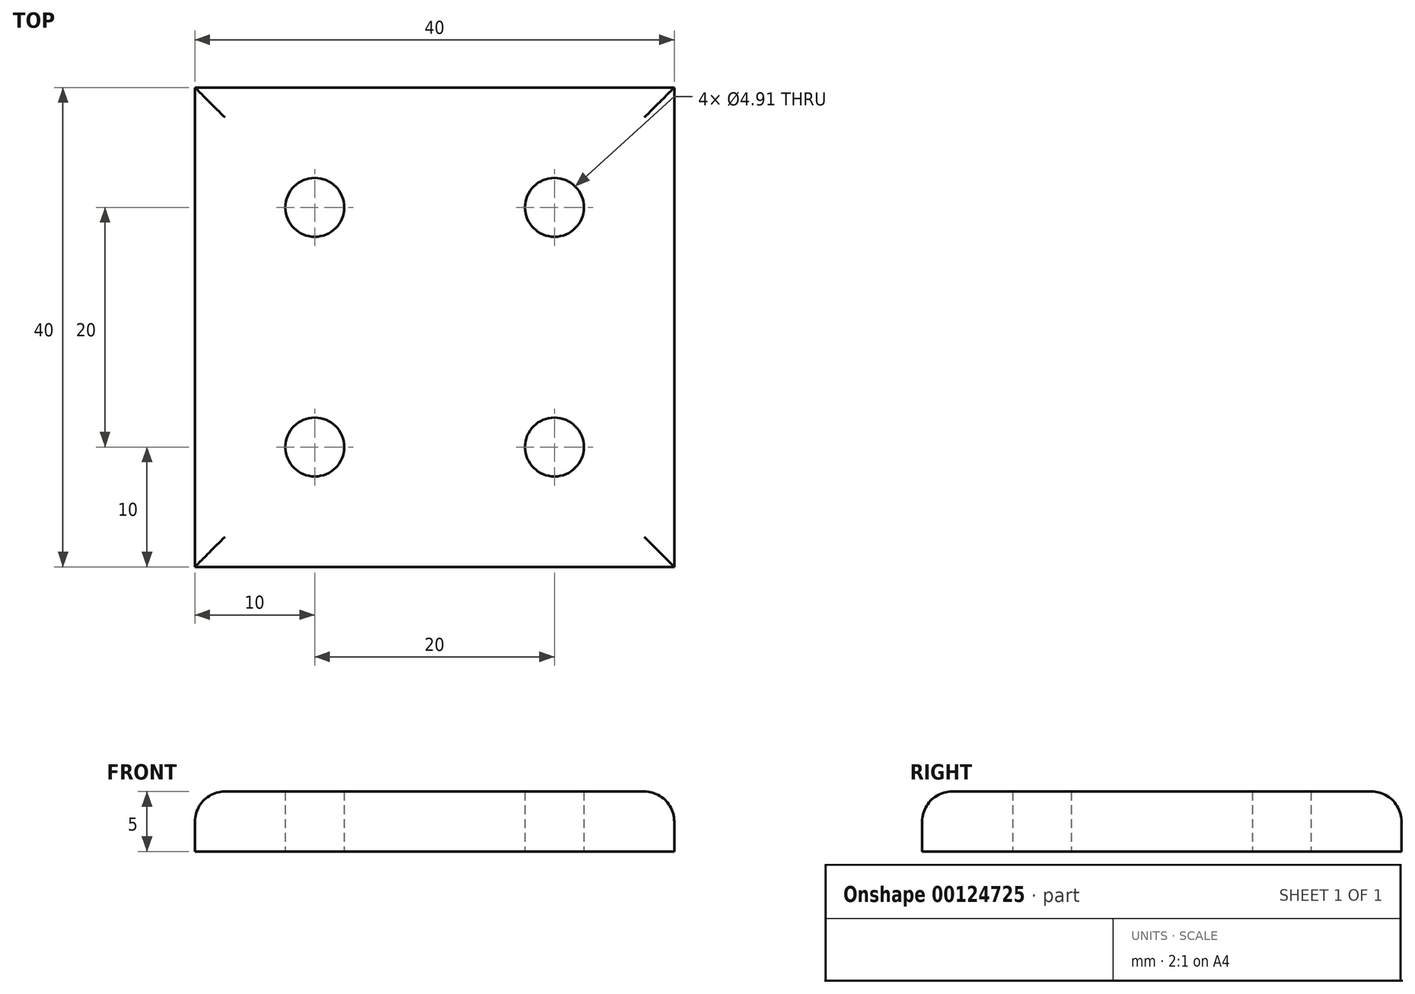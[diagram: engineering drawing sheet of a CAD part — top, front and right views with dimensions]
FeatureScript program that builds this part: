
annotation { "Feature Type Name" : "Feature", "Feature Type Description" : "" }
export const myFeature = defineFeature(function(context is Context, id is Id, definition is map)
    precondition{}
    {
        {
            var Q0;
            Q0=qCreatedBy(makeId("Top.planeOp"),FACE);
            var sketch = newSketch(context, id + "F0", { "sketchPlane" : qUnion([Q0])});
            skLineSegment(sketch, "E0.bottom", {"start": v(-20, 20) * mm, "end": v(20, 20) * mm});
            skLineSegment(sketch, "E0.top", {"start": v(-20, -20) * mm, "end": v(20, -20) * mm});
            skLineSegment(sketch, "E0.left", {"start": v(-20, 20) * mm, "end": v(-20, -20) * mm});
            skLineSegment(sketch, "E0.right", {"start": v(20, 20) * mm, "end": v(20, -20) * mm});
            skPoint(sketch, "E0.middle", {"position": v(0, 0) * mm});
            skCircle(sketch, "E1", {"center": v(-10, 10) * mm, "radius": 2.46 * mm});
            skCircle(sketch, "E2.1.0", {"center": v(-10, -10) * mm, "radius": 2.46 * mm});
            skCircle(sketch, "E2.2.0", {"center": v(10, -10) * mm, "radius": 2.46 * mm});
            skCircle(sketch, "E2.3.0", {"center": v(10, 10) * mm, "radius": 2.46 * mm});
            skSolve(sketch);
        }
        {
            var Q0;
            Q0=makeQuery(id+"F0.imprint","IMPRINT",FACE,{"disambiguationData":[TD([[makeQuery(id+"F0.imprint","IMPRINT",EDGE,{"derivedFrom":sQuery(id+"F0.wireOp",EDGE,"E0.bottom")}),-1.0]])]});
            extrude(context, id + "F1", {"entities" : qUnion([Q0]), "depth" : 5 * mm});
        }
        {
            var Q0;
            Q0=makeQuery(id+"F1.opExtrude","CAP_EDGE",EDGE,{"disambiguationData":[OSD([sQuery(id+"F0.wireOp",EDGE,"E0.top")])],"isStart":false});
            var Q1;
            Q1=makeQuery(id+"F1.opExtrude","CAP_EDGE",EDGE,{"disambiguationData":[OSD([sQuery(id+"F0.wireOp",EDGE,"E0.left")])],"isStart":false});
            var Q2;
            Q2=makeQuery(id+"F1.opExtrude","CAP_EDGE",EDGE,{"disambiguationData":[OSD([sQuery(id+"F0.wireOp",EDGE,"E0.bottom")])],"isStart":false});
            var Q3;
            Q3=makeQuery(id+"F1.opExtrude","CAP_EDGE",EDGE,{"disambiguationData":[OSD([sQuery(id+"F0.wireOp",EDGE,"E0.right")])],"isStart":false});
            fillet(context, id + "F2", {"entities" : qUnion([Q0, Q1, Q2, Q3]), "radius" : 2.5 * mm, "tangentPropagation" : true, "allowEdgeOverflow" : false});
        }
    });
